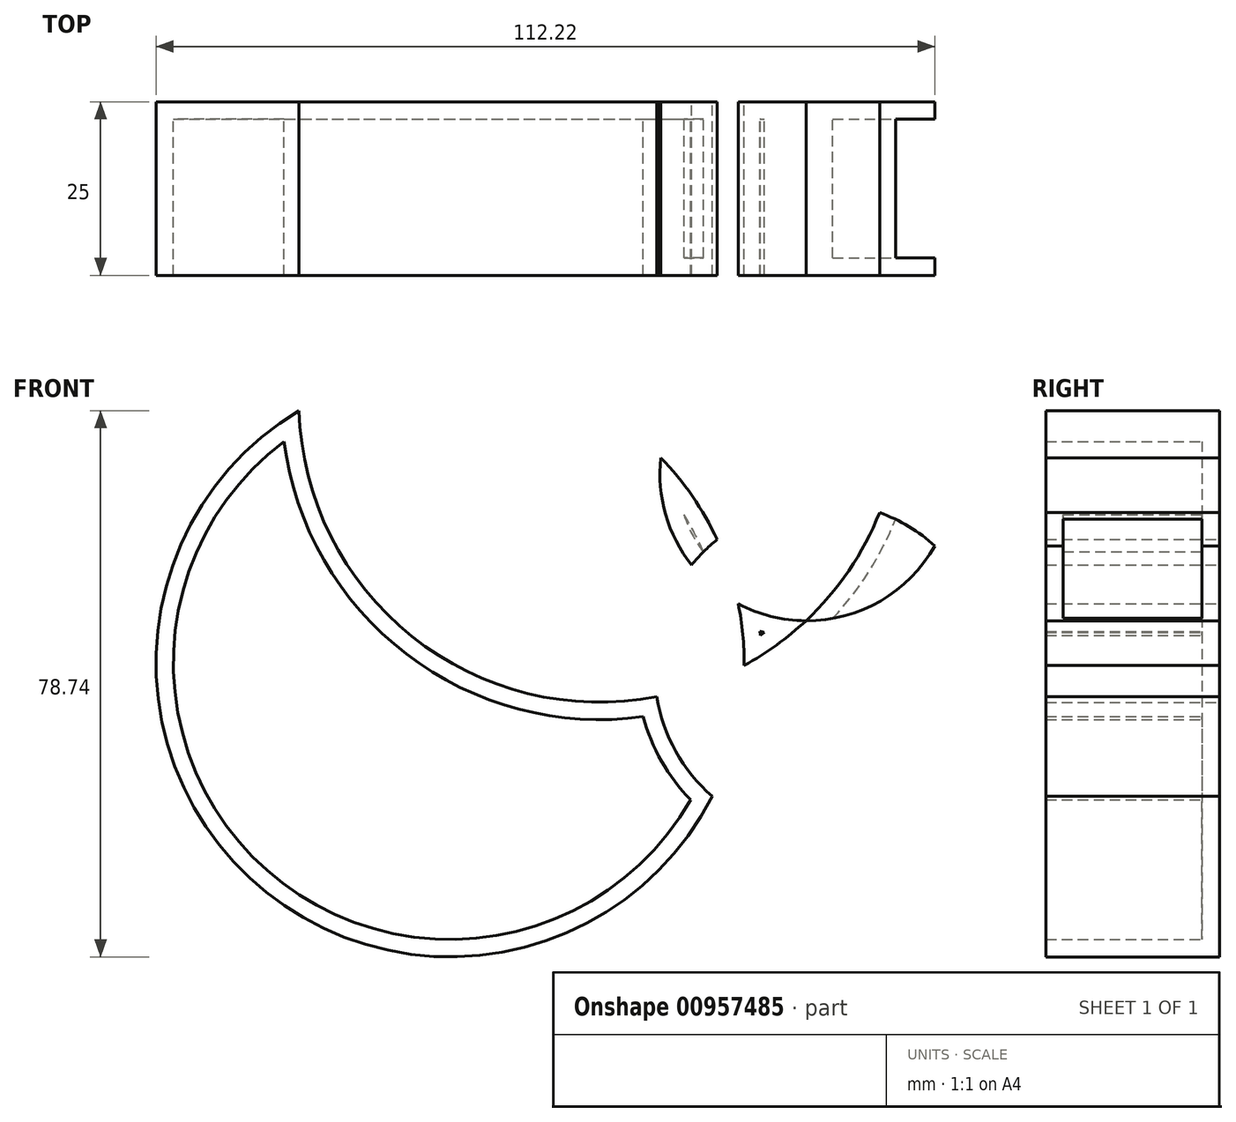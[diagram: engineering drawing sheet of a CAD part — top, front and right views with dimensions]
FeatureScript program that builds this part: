
annotation { "Feature Type Name" : "Feature", "Feature Type Description" : "" }
export const myFeature = defineFeature(function(context is Context, id is Id, definition is map)
    precondition{}
    {
        {
            var Q0;
            Q0=qCreatedBy(makeId("Front.planeOp"),FACE);
            var sketch = newSketch(context, id + "F0", { "sketchPlane" : qUnion([Q0])});
            skCircle(sketch, "E0", {"center": v(49.6, 25.1) * mm, "radius": 21.17 * mm});
            skCircle(sketch, "E1", {"center": v(19.79, 35.55) * mm, "radius": 43.37 * mm});
            skCircle(sketch, "E2", {"center": v(-1.8, -2.14) * mm, "radius": 42.37 * mm});
            skCircle(sketch, "E3", {"center": v(37.6, -24.07) * mm, "radius": 21.64 * mm});
            skCircle(sketch, "E4", {"center": v(51.83, -3.17) * mm, "radius": 24.15 * mm});
            skSolve(sketch);
        }
        {
            var Q0;
            {var subQ0=sQuery(id+"F0.wireOp",EDGE,"E2");var subQ1=sQuery(id+"F0.wireOp",EDGE,"E1");var subQ2=makeQuery(id+"F0.imprint","INTERSECT",VERTEX,{"disambiguationData":[OD(0.0)],"derivedFrom":[subQ1,subQ0]});Q0=makeQuery(id+"F0.imprint","IMPRINT",FACE,{"disambiguationData":[TD([[makeQuery(id+"F0.imprint","IMPRINT",EDGE,{"disambiguationData":[TD([[subQ2,-1.0]])],"derivedFrom":subQ1}),-1.0]])]});}
            var Q1;
            {var subQ0=sQuery(id+"F0.wireOp",EDGE,"E2");var subQ1=sQuery(id+"F0.wireOp",EDGE,"E0");var subQ2=makeQuery(id+"F0.imprint","INTERSECT",VERTEX,{"disambiguationData":[OD(1.0)],"derivedFrom":[subQ1,subQ0]});Q1=makeQuery(id+"F0.imprint","IMPRINT",FACE,{"disambiguationData":[TD([[makeQuery(id+"F0.imprint","IMPRINT",EDGE,{"disambiguationData":[TD([[subQ2,-1.0]])],"derivedFrom":subQ1}),-1.0]])]});}
            var Q2;
            {var subQ0=sQuery(id+"F0.wireOp",EDGE,"E2");var subQ1=sQuery(id+"F0.wireOp",EDGE,"E0");var subQ2=makeQuery(id+"F0.imprint","INTERSECT",VERTEX,{"disambiguationData":[OD(0.0)],"derivedFrom":[subQ1,subQ0]});Q2=makeQuery(id+"F0.imprint","IMPRINT",FACE,{"disambiguationData":[TD([[makeQuery(id+"F0.imprint","IMPRINT",EDGE,{"disambiguationData":[TD([[subQ2,-1.0]])],"derivedFrom":subQ1}),1.0]])]});}
            var Q3;
            {var subQ0=sQuery(id+"F0.wireOp",EDGE,"E3");var subQ1=sQuery(id+"F0.wireOp",EDGE,"E1");var subQ2=makeQuery(id+"F0.imprint","INTERSECT",VERTEX,{"disambiguationData":[OD(0.0)],"derivedFrom":[subQ1,subQ0]});Q3=makeQuery(id+"F0.imprint","IMPRINT",FACE,{"disambiguationData":[TD([[makeQuery(id+"F0.imprint","IMPRINT",EDGE,{"disambiguationData":[TD([[subQ2,-1.0]])],"derivedFrom":subQ1}),-1.0]])]});}
            var Q4;
            {var subQ0=sQuery(id+"F0.wireOp",EDGE,"E4");var subQ1=sQuery(id+"F0.wireOp",EDGE,"E0");var subQ2=makeQuery(id+"F0.imprint","INTERSECT",VERTEX,{"disambiguationData":[OD(0.0)],"derivedFrom":[subQ1,subQ0]});Q4=makeQuery(id+"F0.imprint","IMPRINT",FACE,{"disambiguationData":[TD([[makeQuery(id+"F0.imprint","IMPRINT",EDGE,{"disambiguationData":[TD([[subQ2,1.0]])],"derivedFrom":subQ1}),1.0]])]});}
            extrude(context, id + "F1", {"entities" : qUnion([Q0, Q1, Q2, Q3, Q4]), "depth" : 25 * mm, "offsetDistance" : 25 * mm});
        }
        {
            var Q0;
            Q0=makeQuery(id+"F1.opExtrude","CAP_FACE",FACE,{"disambiguationData":[OSD([sQuery(id+"F0.wireOp",EDGE,"E1"),sQuery(id+"F0.wireOp",EDGE,"E2"),sQuery(id+"F0.wireOp",EDGE,"E4")])],"isStart":false});
            shell(context, id + "F2", {"entities" : qUnion([Q0]), "thickness" : 2.5 * mm});
        }
        {
            var Q0;
            {var subQ0=sQuery(id+"F0.wireOp",EDGE,"E0");Q0=makeQuery(id+"F1.opExtrude","SWEPT_FACE",FACE,{"disambiguationData":[OSD([subQ0]),TDD([makeQuery(id+"F0.imprint","IMPRINT",EDGE,{"disambiguationData":[TD([[makeQuery(id+"F0.imprint","INTERSECT",VERTEX,{"disambiguationData":[OD(0.0)],"derivedFrom":[subQ0,sQuery(id+"F0.wireOp",EDGE,"E4")]}),1.0]])],"derivedFrom":subQ0})])]});}
            var Q1;
            Q1=makeQuery(id+"F1.opExtrude","CAP_FACE",FACE,{"disambiguationData":[OSD([sQuery(id+"F0.wireOp",EDGE,"E0"),sQuery(id+"F0.wireOp",EDGE,"E1"),sQuery(id+"F0.wireOp",EDGE,"E2")])],"isStart":false});
            var Q2;
            {var subQ0=sQuery(id+"F0.wireOp",EDGE,"E4");Q2=makeQuery(id+"F1.opExtrude","SWEPT_FACE",FACE,{"disambiguationData":[OSD([subQ0]),TDD([makeQuery(id+"F0.imprint","IMPRINT",EDGE,{"disambiguationData":[TD([[makeQuery(id+"F0.imprint","INTERSECT",VERTEX,{"disambiguationData":[OD(1.0)],"derivedFrom":[sQuery(id+"F0.wireOp",EDGE,"E0"),subQ0]}),1.0]])],"derivedFrom":subQ0})])]});}
            var Q3;
            {var subQ0=sQuery(id+"F0.wireOp",EDGE,"E4");Q3=makeQuery(id+"F1.opExtrude","SWEPT_FACE",FACE,{"disambiguationData":[OSD([subQ0]),TDD([makeQuery(id+"F0.imprint","IMPRINT",EDGE,{"disambiguationData":[TD([[makeQuery(id+"F0.imprint","INTERSECT",VERTEX,{"disambiguationData":[OD(0.0)],"derivedFrom":[sQuery(id+"F0.wireOp",EDGE,"E0"),subQ0]}),-1.0]])],"derivedFrom":subQ0})])]});}
            shell(context, id + "F3", {"entities" : qUnion([Q0, Q1, Q2, Q3]), "thickness" : 2.5 * mm});
        }
    });
